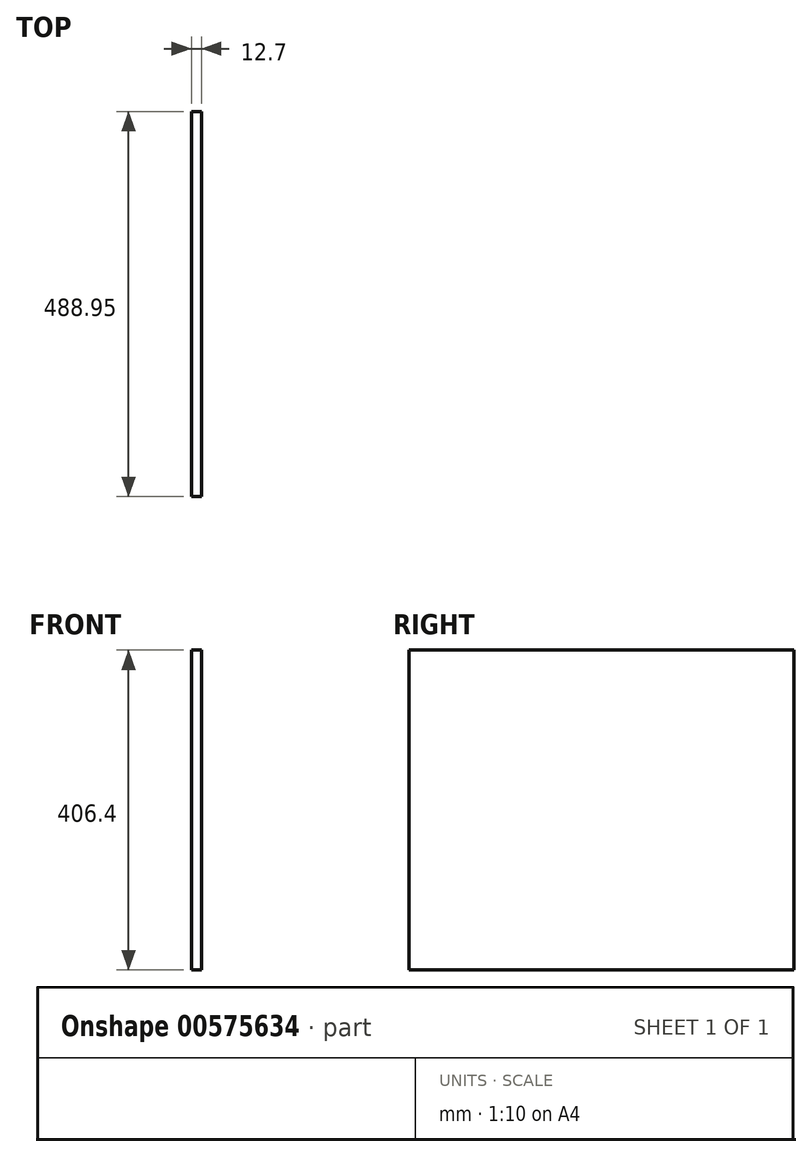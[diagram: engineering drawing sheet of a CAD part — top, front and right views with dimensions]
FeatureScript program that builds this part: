
annotation { "Feature Type Name" : "Feature", "Feature Type Description" : "" }
export const myFeature = defineFeature(function(context is Context, id is Id, definition is map)
    precondition{}
    {
        {
            var Q0;
            Q0=qCreatedBy(makeId("Right.planeOp"),FACE);
            var sketch = newSketch(context, id + "F0", { "sketchPlane" : qUnion([Q0])});
            skLineSegment(sketch, "E0.bottom", {"start": v(-29.78, 408.07) * mm, "end": v(459.17, 408.07) * mm});
            skLineSegment(sketch, "E0.top", {"start": v(-29.78, 1.67) * mm, "end": v(459.17, 1.67) * mm});
            skLineSegment(sketch, "E0.left", {"start": v(-29.78, 408.07) * mm, "end": v(-29.78, 1.67) * mm});
            skLineSegment(sketch, "E0.right", {"start": v(459.17, 408.07) * mm, "end": v(459.17, 1.67) * mm});
            skSolve(sketch);
        }
        {
            var Q0;
            Q0=qSketchRegion(id+"F0",true);
            extrude(context, id + "F1", {"entities" : qUnion([Q0]), "depth" : 12.7 * mm, "offsetDistance" : 25.4 * mm});
        }
    });
